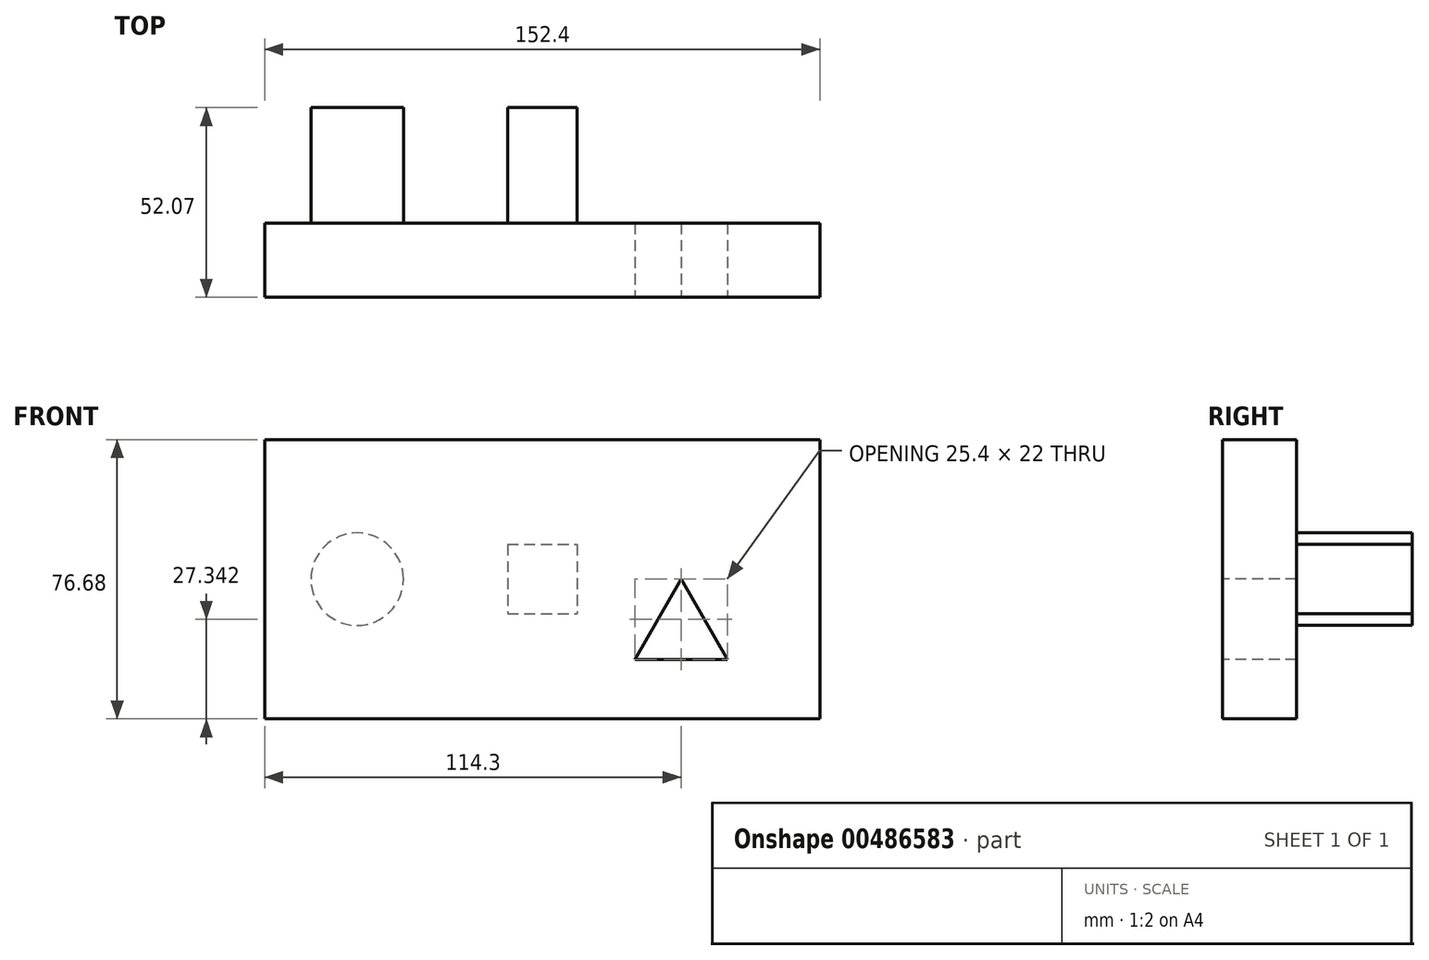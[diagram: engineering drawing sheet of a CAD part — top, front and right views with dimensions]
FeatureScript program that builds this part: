
annotation { "Feature Type Name" : "Feature", "Feature Type Description" : "" }
export const myFeature = defineFeature(function(context is Context, id is Id, definition is map)
    precondition{}
    {
        {
            var Q0;
            Q0=qCreatedBy(makeId("Front.planeOp"),FACE);
            var sketch = newSketch(context, id + "F0", { "sketchPlane" : qUnion([Q0])});
            skLineSegment(sketch, "E0", {"start": v(0, 0) * mm, "end": v(6.35, 0) * mm});
            skLineSegment(sketch, "E1", {"start": v(6.35, 0) * mm, "end": v(-6.35, -22) * mm});
            skLineSegment(sketch, "E2", {"start": v(-6.35, -22) * mm, "end": v(19.05, -22) * mm});
            skLineSegment(sketch, "E3", {"start": v(19.05, -22) * mm, "end": v(6.35, 0) * mm});
            skLineSegment(sketch, "E4", {"start": v(0, 0) * mm, "end": v(-31.75, 0) * mm});
            skLineSegment(sketch, "E5.bottom", {"start": v(-41.27, 9.53) * mm, "end": v(-22.22, 9.53) * mm});
            skLineSegment(sketch, "E5.top", {"start": v(-41.28, -9.52) * mm, "end": v(-22.22, -9.52) * mm});
            skLineSegment(sketch, "E5.left", {"start": v(-41.27, 9.53) * mm, "end": v(-41.28, -9.52) * mm});
            skLineSegment(sketch, "E5.right", {"start": v(-22.22, 9.53) * mm, "end": v(-22.22, -9.52) * mm});
            skPoint(sketch, "E5.middle", {"position": v(-31.75, 0) * mm});
            skLineSegment(sketch, "E6", {"start": v(-31.75, 0) * mm, "end": v(-82.55, 0) * mm});
            skCircle(sketch, "E7", {"center": v(-82.55, 0) * mm, "radius": 12.7 * mm});
            skLineSegment(sketch, "E8.bottom", {"start": v(-107.95, 38.34) * mm, "end": v(44.45, 38.34) * mm});
            skLineSegment(sketch, "E8.top", {"start": v(-107.95, -38.34) * mm, "end": v(44.45, -38.34) * mm});
            skLineSegment(sketch, "E8.left", {"start": v(-107.95, 38.34) * mm, "end": v(-107.95, -38.34) * mm});
            skLineSegment(sketch, "E8.right", {"start": v(44.45, 38.34) * mm, "end": v(44.45, -38.34) * mm});
            skSolve(sketch);
        }
        {
            var Q0;
            Q0=makeQuery(id+"F0.imprint","IMPRINT",FACE,{"disambiguationData":[TD([[makeQuery(id+"F0.imprint","IMPRINT",EDGE,{"derivedFrom":sQuery(id+"F0.wireOp",EDGE,"E1")}),-1.0]])]});
            extrude(context, id + "F1", {"entities" : qUnion([Q0]), "oppositeDirection" : true, "depth" : 20.32 * mm});
        }
        {
            var Q0;
            {var subQ1=sQuery(id+"F0.wireOp",EDGE,"E5.top");Q0=makeQuery(id+"F0.imprint","IMPRINT",FACE,{"disambiguationData":[TD([[makeQuery(id+"F0.imprint","IMPRINT",EDGE,{"derivedFrom":subQ1}),1.0]])]});}
            var Q1;
            {var subQ1=sQuery(id+"F0.wireOp",EDGE,"E5.bottom");Q1=makeQuery(id+"F0.imprint","IMPRINT",FACE,{"disambiguationData":[TD([[makeQuery(id+"F0.imprint","IMPRINT",EDGE,{"derivedFrom":subQ1}),-1.0]])]});}
            var Q2;
            Q2=makeQuery(id+"F0.imprint","IMPRINT",FACE,{"disambiguationData":[TD([[makeQuery(id+"F0.imprint","IMPRINT",EDGE,{"derivedFrom":sQuery(id+"F0.wireOp",EDGE,"E7")}),1.0]])]});
            extrude(context, id + "F2", {"entities" : qUnion([Q0, Q1, Q2]), "operationType" : NewBodyOperationType.ADD, "oppositeDirection" : true, "depth" : 52.07 * mm});
        }
    });
